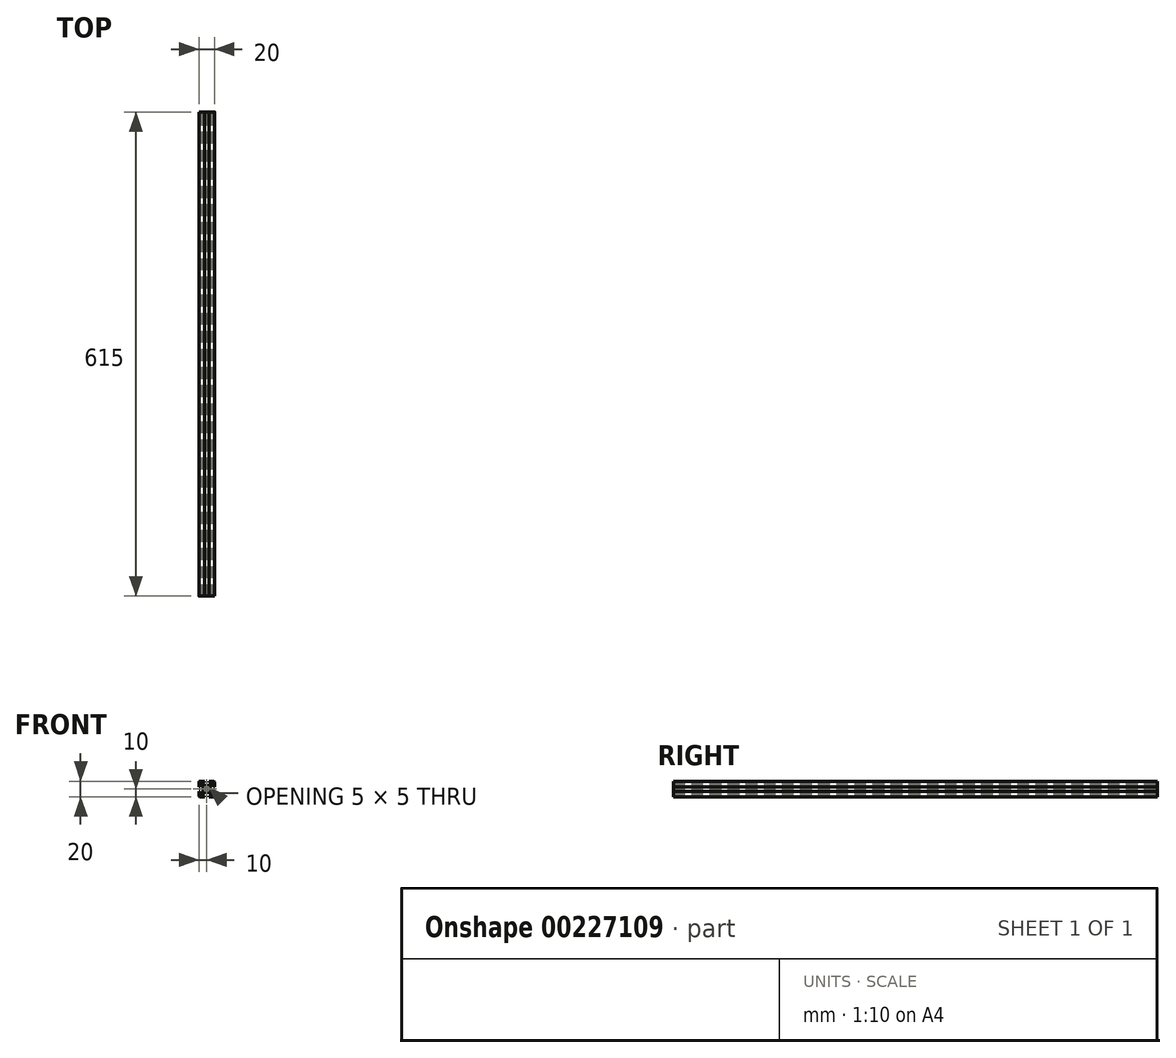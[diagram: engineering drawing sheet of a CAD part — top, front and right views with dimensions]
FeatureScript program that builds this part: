
annotation { "Feature Type Name" : "Feature", "Feature Type Description" : "" }
export const myFeature = defineFeature(function(context is Context, id is Id, definition is map)
    precondition{}
    {
        {
            var Q0;
            Q0=qCreatedBy(makeId("Front.planeOp"),FACE);
            var sketch = newSketch(context, id + "F0", { "sketchPlane" : qUnion([Q0])});
            skLineSegment(sketch, "E0.bottom", {"start": v(8.5, -10) * mm, "end": v(3, -10) * mm});
            skLineSegment(sketch, "E0.top", {"start": v(8.5, 10) * mm, "end": v(3, 10) * mm});
            skLineSegment(sketch, "E0.left", {"start": v(10, -8.5) * mm, "end": v(10, -3) * mm});
            skLineSegment(sketch, "E0.right", {"start": v(-10, -8.5) * mm, "end": v(-10, -3) * mm});
            skPoint(sketch, "E0.middle", {"position": v(0, 0) * mm});
            skLineSegment(sketch, "E1.bottom", {"start": v(6, -8.5) * mm, "end": v(3, -8.5) * mm});
            skLineSegment(sketch, "E1.top", {"start": v(6, 8.5) * mm, "end": v(3, 8.5) * mm});
            skLineSegment(sketch, "E1.left", {"start": v(8.5, -6) * mm, "end": v(8.5, -3) * mm});
            skLineSegment(sketch, "E1.right", {"start": v(-8.5, -6) * mm, "end": v(-8.5, -3) * mm});
            skLineSegment(sketch, "E2.bottom", {"start": v(3.44, -4.5) * mm, "end": v(-3.44, -4.5) * mm});
            skLineSegment(sketch, "E2.top", {"start": v(3.44, 4.5) * mm, "end": v(-3.44, 4.5) * mm});
            skLineSegment(sketch, "E2.left", {"start": v(4.5, -3.44) * mm, "end": v(4.5, 3.44) * mm});
            skLineSegment(sketch, "E2.right", {"start": v(-4.5, -3.44) * mm, "end": v(-4.5, 3.44) * mm});
            skLineSegment(sketch, "E3.bottom", {"start": v(8.5, -6) * mm, "end": v(7.06, -6) * mm});
            skLineSegment(sketch, "E3.top", {"start": v(8.5, 6) * mm, "end": v(7.06, 6) * mm});
            skLineSegment(sketch, "E4.left", {"start": v(6, -8.5) * mm, "end": v(6, -7.06) * mm});
            skLineSegment(sketch, "E4.right", {"start": v(-6, -8.5) * mm, "end": v(-6, -7.06) * mm});
            skPoint(sketch, "E5.orphan", {"position": v(-8.5, 8.5) * mm});
            skPoint(sketch, "E6.orphan", {"position": v(8.5, 8.5) * mm});
            skPoint(sketch, "E7.orphan", {"position": v(8.5, -8.5) * mm});
            skPoint(sketch, "E8.orphan", {"position": v(-8.5, -8.5) * mm});
            skLineSegment(sketch, "E9.trimOffspring", {"start": v(-6, 7.06) * mm, "end": v(-6, 8.5) * mm});
            skLineSegment(sketch, "E10.trimOffspring", {"start": v(-7.06, 6) * mm, "end": v(-8.5, 6) * mm});
            skLineSegment(sketch, "E11.trimOffspring", {"start": v(6, 7.06) * mm, "end": v(6, 8.5) * mm});
            skLineSegment(sketch, "E12.trimOffspring", {"start": v(-7.06, -6) * mm, "end": v(-8.5, -6) * mm});
            skLineSegment(sketch, "E13", {"start": v(-10, 10) * mm, "end": v(0, 0) * mm, "construction": true});
            skLineSegment(sketch, "E14", {"start": v(10, 10) * mm, "end": v(0, 0) * mm, "construction": true});
            skLineSegment(sketch, "E15", {"start": v(-6, 7.06) * mm, "end": v(-3.44, 4.5) * mm});
            skPoint(sketch, "E15.endSnap0", {"position": v(7.25, -6) * mm});
            skLineSegment(sketch, "E16", {"start": v(6, -7.06) * mm, "end": v(3.44, -4.5) * mm});
            skLineSegment(sketch, "E17", {"start": v(7.06, 6) * mm, "end": v(4.5, 3.44) * mm});
            skLineSegment(sketch, "E18", {"start": v(6, 7.06) * mm, "end": v(3.44, 4.5) * mm});
            skPoint(sketch, "E19.orphan", {"position": v(6, -6) * mm});
            skPoint(sketch, "E20.orphan", {"position": v(-4.5, -4.5) * mm});
            skPoint(sketch, "E21.orphan", {"position": v(-4.5, 4.5) * mm});
            skPoint(sketch, "E22.orphan", {"position": v(4.5, 4.5) * mm});
            skPoint(sketch, "E23.orphan", {"position": v(4.5, -4.5) * mm});
            skLineSegment(sketch, "E24.trimOffspring", {"start": v(4.5, -3.44) * mm, "end": v(7.06, -6) * mm});
            skLineSegment(sketch, "E25.trimOffspring", {"start": v(-3.44, -4.5) * mm, "end": v(-6, -7.06) * mm});
            skLineSegment(sketch, "E26.trimOffspring", {"start": v(-4.5, -3.44) * mm, "end": v(-7.06, -6) * mm});
            skLineSegment(sketch, "E27.trimOffspring", {"start": v(-4.5, 3.44) * mm, "end": v(-7.06, 6) * mm});
            skLineSegment(sketch, "E28.bottom", {"start": v(8.5, -3) * mm, "end": v(10, -3) * mm});
            skLineSegment(sketch, "E28.top", {"start": v(8.5, 3) * mm, "end": v(10, 3) * mm});
            skPoint(sketch, "E28.middle", {"position": v(10, 0) * mm});
            skLineSegment(sketch, "E29.left", {"start": v(3, 8.5) * mm, "end": v(3, 10) * mm});
            skLineSegment(sketch, "E29.right", {"start": v(-3, 8.5) * mm, "end": v(-3, 10) * mm});
            skPoint(sketch, "E29.middle", {"position": v(0, 10) * mm});
            skLineSegment(sketch, "E30.bottom", {"start": v(-8.5, 3) * mm, "end": v(-10, 3) * mm});
            skLineSegment(sketch, "E30.top", {"start": v(-8.5, -3) * mm, "end": v(-10, -3) * mm});
            skPoint(sketch, "E30.middle", {"position": v(-10, 0) * mm});
            skLineSegment(sketch, "E31.left", {"start": v(3, -8.5) * mm, "end": v(3, -10) * mm});
            skLineSegment(sketch, "E31.right", {"start": v(-3, -8.5) * mm, "end": v(-3, -10) * mm});
            skPoint(sketch, "E31.middle", {"position": v(0, -10) * mm});
            skPoint(sketch, "E32.orphan", {"position": v(3, 11.5) * mm});
            skPoint(sketch, "E33.orphan", {"position": v(-3, 11.5) * mm});
            skLineSegment(sketch, "E34.trimOffspring", {"start": v(-3, 10) * mm, "end": v(-8.5, 10) * mm});
            skLineSegment(sketch, "E35.trimOffspring", {"start": v(-3, 8.5) * mm, "end": v(-6, 8.5) * mm});
            skPoint(sketch, "E28.right.end.orphan", {"position": v(11.5, 3) * mm});
            skPoint(sketch, "E36.orphan", {"position": v(11.5, -3) * mm});
            skLineSegment(sketch, "E37.trimOffspring", {"start": v(10, 3) * mm, "end": v(10, 8.5) * mm});
            skLineSegment(sketch, "E38.trimOffspring", {"start": v(8.5, 3) * mm, "end": v(8.5, 6) * mm});
            skPoint(sketch, "E39.orphan", {"position": v(3, -11.5) * mm});
            skPoint(sketch, "E40.orphan", {"position": v(-3, -11.5) * mm});
            skLineSegment(sketch, "E41.trimOffspring", {"start": v(-3, -10) * mm, "end": v(-8.5, -10) * mm});
            skLineSegment(sketch, "E42.trimOffspring", {"start": v(-3, -8.5) * mm, "end": v(-6, -8.5) * mm});
            skPoint(sketch, "E30.right.end.orphan", {"position": v(-11.5, -3) * mm});
            skPoint(sketch, "E43.orphan", {"position": v(-11.5, 3) * mm});
            skLineSegment(sketch, "E44.trimOffspring", {"start": v(-10, 3) * mm, "end": v(-10, 8.5) * mm});
            skLineSegment(sketch, "E45.trimOffspring", {"start": v(-8.5, 3) * mm, "end": v(-8.5, 6) * mm});
            skLineSegment(sketch, "E46.trimOffspring", {"start": v(0, 0) * mm, "end": v(10, -10) * mm, "construction": true});
            skLineSegment(sketch, "E47.trimOffspring", {"start": v(0, 0) * mm, "end": v(-10, -10) * mm, "construction": true});
            skArc(sketch, "E48", {"start": v(1.16, 2.22) * mm, "mid": v(0, 2.5) * mm, "end": v(-1.16, 2.22) * mm});
            skLineSegment(sketch, "E49", {"start": v(-2.5, -1.44) * mm, "end": v(1.44, 2.5) * mm});
            skLineSegment(sketch, "E50", {"start": v(2.5, 1.44) * mm, "end": v(-1.44, -2.5) * mm});
            skLineSegment(sketch, "E51", {"start": v(1.44, -2.5) * mm, "end": v(-2.5, 1.44) * mm});
            skLineSegment(sketch, "E52", {"start": v(-1.44, 2.5) * mm, "end": v(2.5, -1.44) * mm});
            skLineSegment(sketch, "E53", {"start": v(2.5, 1.44) * mm, "end": v(2.5, -1.44) * mm, "construction": true});
            skLineSegment(sketch, "E54", {"start": v(1.44, -2.5) * mm, "end": v(-1.44, -2.5) * mm, "construction": true});
            skLineSegment(sketch, "E55", {"start": v(-2.5, -1.44) * mm, "end": v(-2.5, 1.44) * mm, "construction": true});
            skLineSegment(sketch, "E56", {"start": v(-1.44, 2.5) * mm, "end": v(1.44, 2.5) * mm, "construction": true});
            skLineSegment(sketch, "E57", {"start": v(-1.44, 2.5) * mm, "end": v(-2.5, 1.44) * mm});
            skLineSegment(sketch, "E58", {"start": v(1.44, 2.5) * mm, "end": v(2.5, 1.44) * mm});
            skLineSegment(sketch, "E59", {"start": v(2.5, -1.44) * mm, "end": v(1.44, -2.5) * mm});
            skLineSegment(sketch, "E60", {"start": v(-1.44, -2.5) * mm, "end": v(-2.5, -1.44) * mm});
            skArc(sketch, "E61.trimOffspring", {"start": v(-2.22, 1.16) * mm, "mid": v(-2.5, 0) * mm, "end": v(-2.22, -1.16) * mm});
            skArc(sketch, "E62.trimOffspring", {"start": v(-1.16, -2.22) * mm, "mid": v(0, -2.5) * mm, "end": v(1.16, -2.22) * mm});
            skArc(sketch, "E63.trimOffspring", {"start": v(2.22, -1.16) * mm, "mid": v(2.5, 0) * mm, "end": v(2.22, 1.16) * mm});
            skPoint(sketch, "E64.visualSharp", {"position": v(10, 10) * mm});
            skArc(sketch, "E64.filletArc", {"start": v(10, 8.5) * mm, "mid": v(9.56, 9.56) * mm, "end": v(8.5, 10) * mm});
            skPoint(sketch, "E65.visualSharp", {"position": v(10, -10) * mm});
            skArc(sketch, "E65.filletArc", {"start": v(8.5, -10) * mm, "mid": v(9.56, -9.56) * mm, "end": v(10, -8.5) * mm});
            skPoint(sketch, "E66.visualSharp", {"position": v(-10, -10) * mm});
            skArc(sketch, "E66.filletArc", {"start": v(-10, -8.5) * mm, "mid": v(-9.56, -9.56) * mm, "end": v(-8.5, -10) * mm});
            skPoint(sketch, "E67.visualSharp", {"position": v(-10, 10) * mm});
            skArc(sketch, "E67.filletArc", {"start": v(-8.5, 10) * mm, "mid": v(-9.56, 9.56) * mm, "end": v(-10, 8.5) * mm});
            skSolve(sketch);
        }
        {
            assignVariable(context, id + "F2", {"name" : "Length", "anyValue" : 615});
        }
        {
            var Q0;
            Q0=qSketchRegion(id+"F0",true);
            extrude(context, id + "F1", {"entities" : qUnion([Q0]), "depth" : (getVariable(context, 'Length')) * mm});
        }
    });
